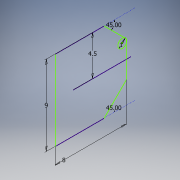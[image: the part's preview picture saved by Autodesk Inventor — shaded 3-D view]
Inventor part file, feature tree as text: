
AUTODESK INVENTOR PART (.ipt)
format: ipt  version: 2018 (Build 220112000, 112)  size: 94,720 bytes
history: native  units: mm
features: sketch x1
ambient origin geometry x8: Origin, YZ Plane, XZ Plane, XY Plane, X Axis, Y Axis, Z Axis, Center Point
feature tree (1):
  sketch  "Sketch1"  dims[d0=9.0mm d1=4.5mm d7=45.0deg d9=45.0deg d11=8.0mm d13=1.0mm]
